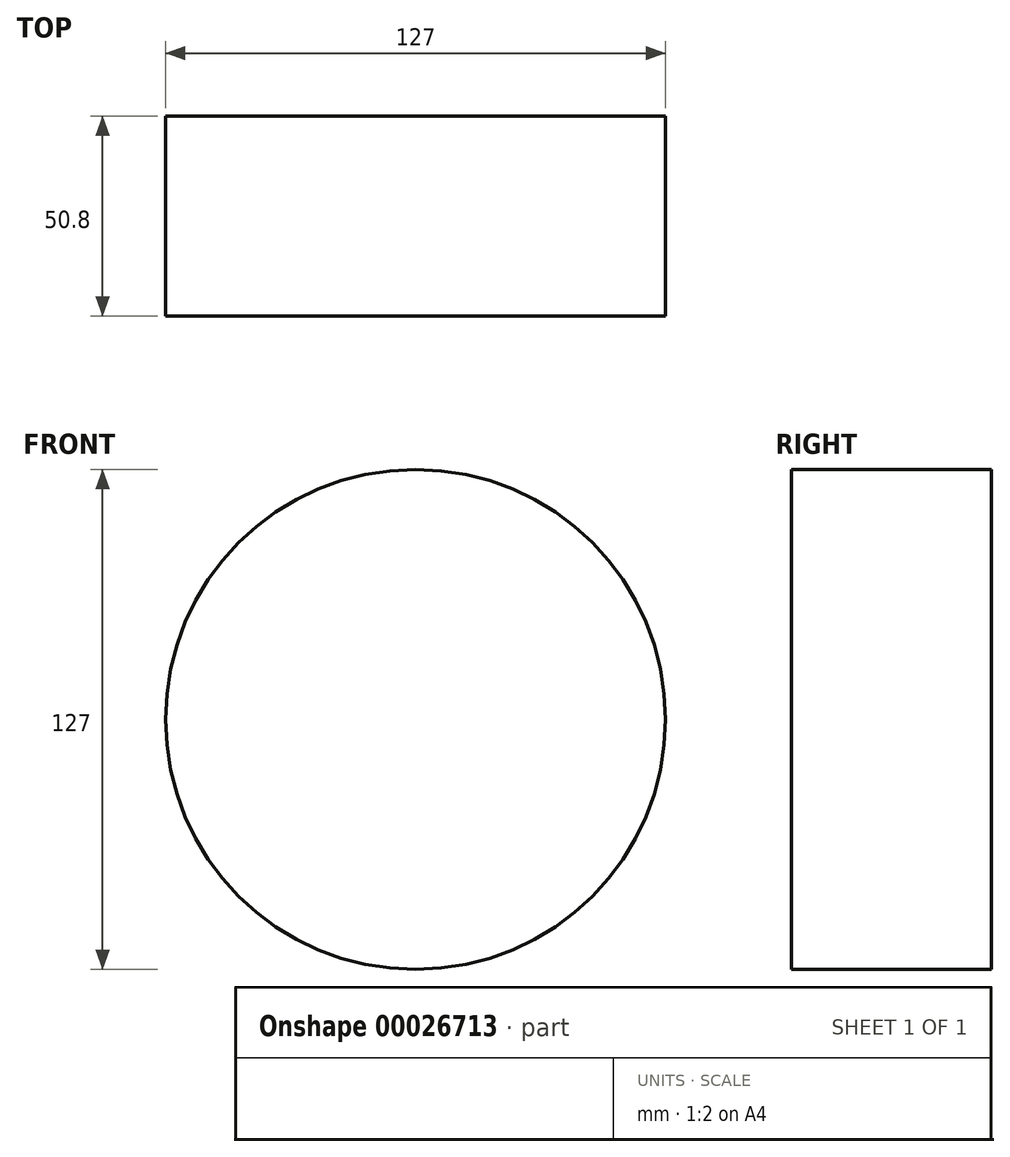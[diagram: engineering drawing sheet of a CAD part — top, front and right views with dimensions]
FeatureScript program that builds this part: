
annotation { "Feature Type Name" : "Feature", "Feature Type Description" : "" }
export const myFeature = defineFeature(function(context is Context, id is Id, definition is map)
    precondition{}
    {
        {
            var Q0;
            Q0=qCreatedBy(makeId("Front.planeOp"),FACE);
            var sketch = newSketch(context, id + "F0", { "sketchPlane" : qUnion([Q0])});
            skCircle(sketch, "E0", {"center": v(-11.37, 11.94) * mm, "radius": 63.5 * mm});
            skSolve(sketch);
        }
        {
            var Q0;
            Q0 = qSketchRegion(id + "F0", true);
            extrude(context, id + "F1", {"entities" : qUnion([Q0]), "depth" : 50.8 * mm});
        }
    });
